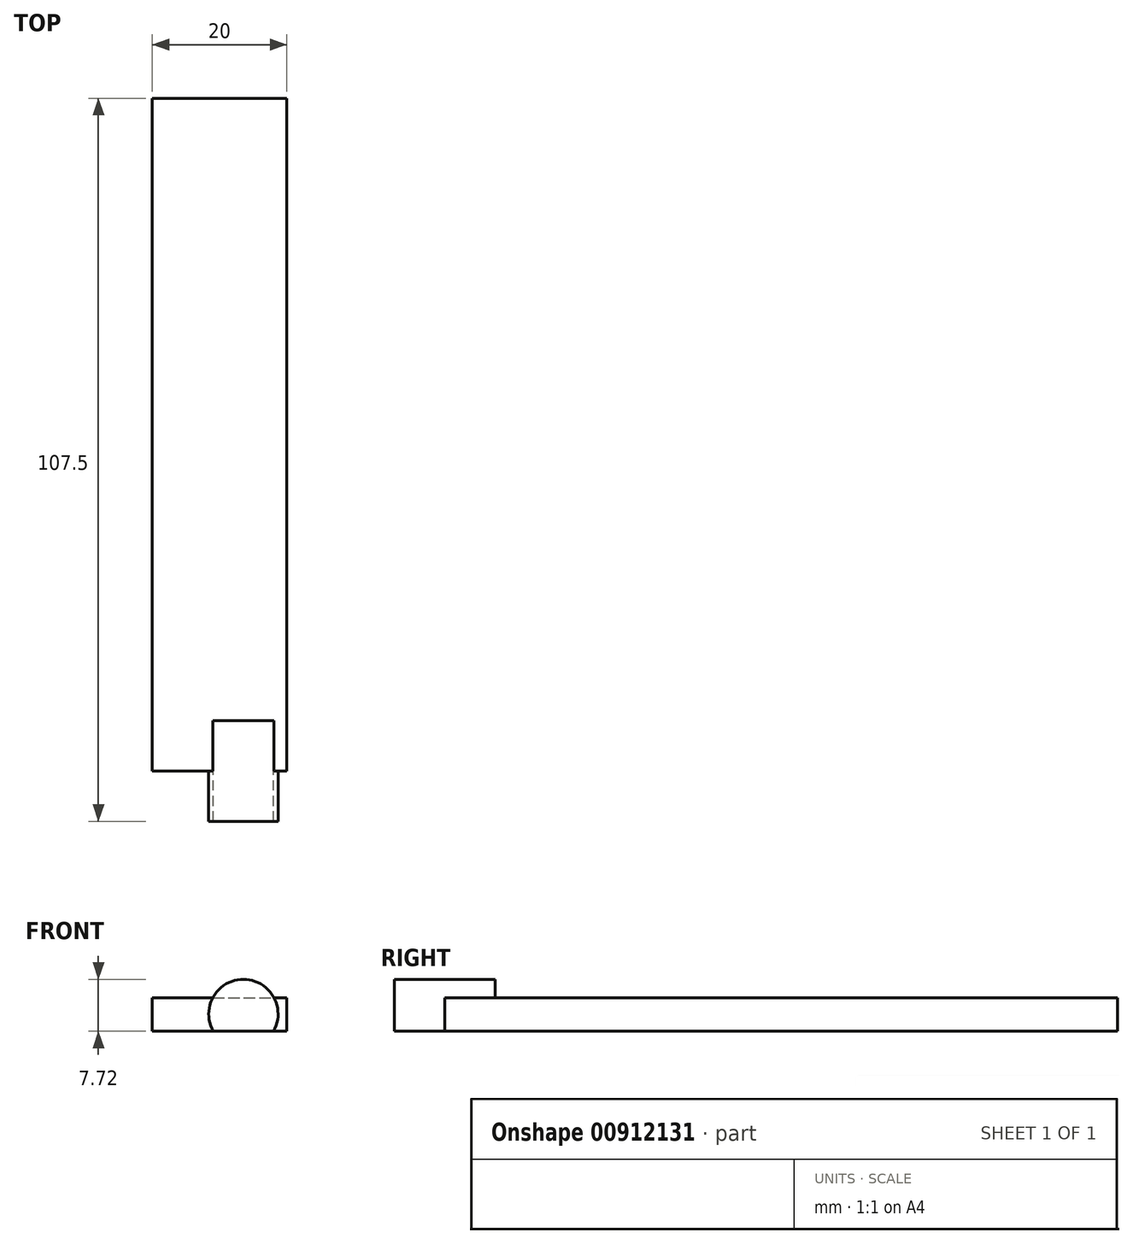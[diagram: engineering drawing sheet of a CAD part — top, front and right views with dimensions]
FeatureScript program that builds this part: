
annotation { "Feature Type Name" : "Feature", "Feature Type Description" : "" }
export const myFeature = defineFeature(function(context is Context, id is Id, definition is map)
    precondition{}
    {
        {
            var Q0;
            Q0=qCreatedBy(makeId("Top.planeOp"),FACE);
            var sketch = newSketch(context, id + "F0", { "sketchPlane" : qUnion([Q0])});
            skLineSegment(sketch, "E0.bottom", {"start": v(-9.9, 51.18) * mm, "end": v(10.1, 51.18) * mm});
            skLineSegment(sketch, "E0.top", {"start": v(-9.9, -48.82) * mm, "end": v(10.1, -48.82) * mm});
            skLineSegment(sketch, "E0.left", {"start": v(-9.9, 51.18) * mm, "end": v(-9.9, -48.82) * mm});
            skLineSegment(sketch, "E0.right", {"start": v(10.1, 51.18) * mm, "end": v(10.1, -48.82) * mm});
            skSolve(sketch);
        }
        {
            var Q0;
            Q0=makeQuery(id+"F0.imprint","IMPRINT",FACE,{"disambiguationData":[TD([[makeQuery(id+"F0.imprint","IMPRINT",EDGE,{"derivedFrom":sQuery(id+"F0.wireOp",EDGE,"E0.bottom")}),-1.0]])]});
            extrude(context, id + "F1", {"entities" : qUnion([Q0]), "depth" : 5 * mm, "offsetDistance" : 25 * mm});
        }
        {
            var Q0;
            Q0=makeQuery(id+"F1.opExtrude","SWEPT_FACE",FACE,{"disambiguationData":[OSD([sQuery(id+"F0.wireOp",EDGE,"E0.top")])]});
            var sketch = newSketch(context, id + "F2", { "sketchPlane" : qUnion([Q0])});
            skCircle(sketch, "E1", {"center": v(3.63, 2.56) * mm, "radius": 5.16 * mm});
            skSolve(sketch);
        }
        {
            var Q0;
            {var subQ0=sQuery(id+"F2.wireOp",EDGE,"E1");var subQ1=sQuery(id+"F0.wireOp",EDGE,"E0.top");var subQ2=makeQuery(id+"F1.opExtrude","CAP_EDGE",EDGE,{"disambiguationData":[OSD([subQ1])],"isStart":false});var subQ3=makeQuery(id+"F2.imprint","INTERSECT",VERTEX,{"disambiguationData":[OD(0.0)],"derivedFrom":[subQ2,subQ0]});Q0=makeQuery(id+"F2.imprint","IMPRINT",FACE,{"disambiguationData":[TD([[makeQuery(id+"F2.imprint","IMPRINT",EDGE,{"disambiguationData":[TD([[subQ3,-1.0]])],"derivedFrom":subQ0}),1.0]])]});}
            var Q1;
            {var subQ0=sQuery(id+"F2.wireOp",EDGE,"E1");var subQ1=makeQuery(id+"F1.opExtrude","CAP_EDGE",EDGE,{"disambiguationData":[OSD([sQuery(id+"F0.wireOp",EDGE,"E0.top")])],"isStart":false});var subQ2=makeQuery(id+"F2.imprint","INTERSECT",VERTEX,{"disambiguationData":[OD(0.0)],"derivedFrom":[subQ1,subQ0]});Q1=makeQuery(id+"F2.imprint","IMPRINT",FACE,{"disambiguationData":[TD([[makeQuery(id+"F2.imprint","IMPRINT",EDGE,{"disambiguationData":[TD([[subQ2,1.0]])],"derivedFrom":subQ0}),1.0]])]});}
            var Q2;
            {var subQ0=sQuery(id+"F2.wireOp",EDGE,"E1");var subQ1=makeQuery(id+"F1.opExtrude","CAP_EDGE",EDGE,{"disambiguationData":[OSD([sQuery(id+"F0.wireOp",EDGE,"E0.top")])],"isStart":true});var subQ2=makeQuery(id+"F2.imprint","INTERSECT",VERTEX,{"disambiguationData":[OD(0.0)],"derivedFrom":[subQ1,subQ0]});Q2=makeQuery(id+"F2.imprint","IMPRINT",FACE,{"disambiguationData":[TD([[makeQuery(id+"F2.imprint","IMPRINT",EDGE,{"disambiguationData":[TD([[subQ2,-1.0]])],"derivedFrom":subQ0}),1.0]])]});}
            extrude(context, id + "F3", {"entities" : qUnion([Q0, Q1, Q2]), "operationType" : NewBodyOperationType.ADD, "endBound" : BoundingType.SYMMETRIC, "depth" : 15 * mm, "offsetDistance" : 25 * mm});
        }
    });
